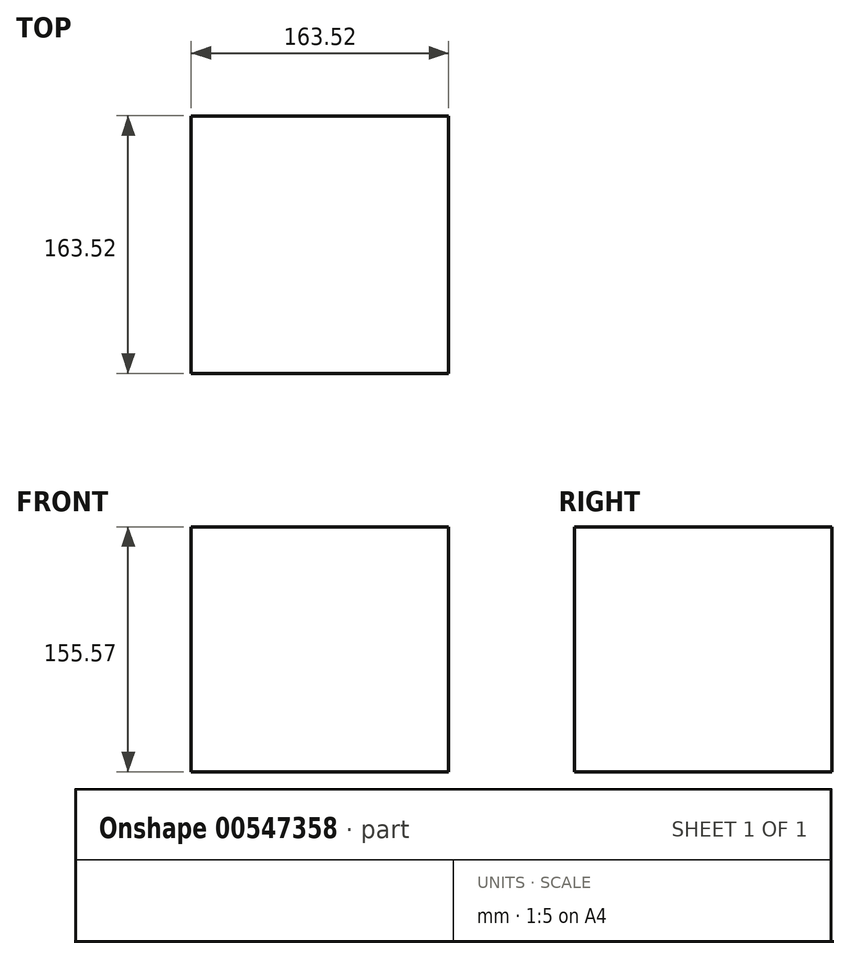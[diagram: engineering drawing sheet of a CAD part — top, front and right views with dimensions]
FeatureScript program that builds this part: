
annotation { "Feature Type Name" : "Feature", "Feature Type Description" : "" }
export const myFeature = defineFeature(function(context is Context, id is Id, definition is map)
    precondition{}
    {
        {
            var Q0;
            Q0=qCreatedBy(makeId("Top.planeOp"),FACE);
            var sketch = newSketch(context, id + "F0", { "sketchPlane" : qUnion([Q0])});
            skLineSegment(sketch, "E0.bottom", {"start": v(81.76, 81.76) * mm, "end": v(-81.76, 81.76) * mm});
            skLineSegment(sketch, "E0.top", {"start": v(81.76, -81.76) * mm, "end": v(-81.76, -81.76) * mm});
            skLineSegment(sketch, "E0.left", {"start": v(81.76, 81.76) * mm, "end": v(81.76, -81.76) * mm});
            skLineSegment(sketch, "E0.right", {"start": v(-81.76, 81.76) * mm, "end": v(-81.76, -81.76) * mm});
            skPoint(sketch, "E0.middle", {"position": v(0, 0) * mm});
            skSolve(sketch);
        }
        {
            var Q0;
            Q0=makeQuery(id+"F0.imprint","IMPRINT",FACE,{"disambiguationData":[TD([[makeQuery(id+"F0.imprint","IMPRINT",EDGE,{"derivedFrom":sQuery(id+"F0.wireOp",EDGE,"E0.bottom")}),1.0]])]});
            extrude(context, id + "F1", {"entities" : qUnion([Q0]), "depth" : 155.57 * mm, "offsetDistance" : 25.4 * mm});
        }
    });
